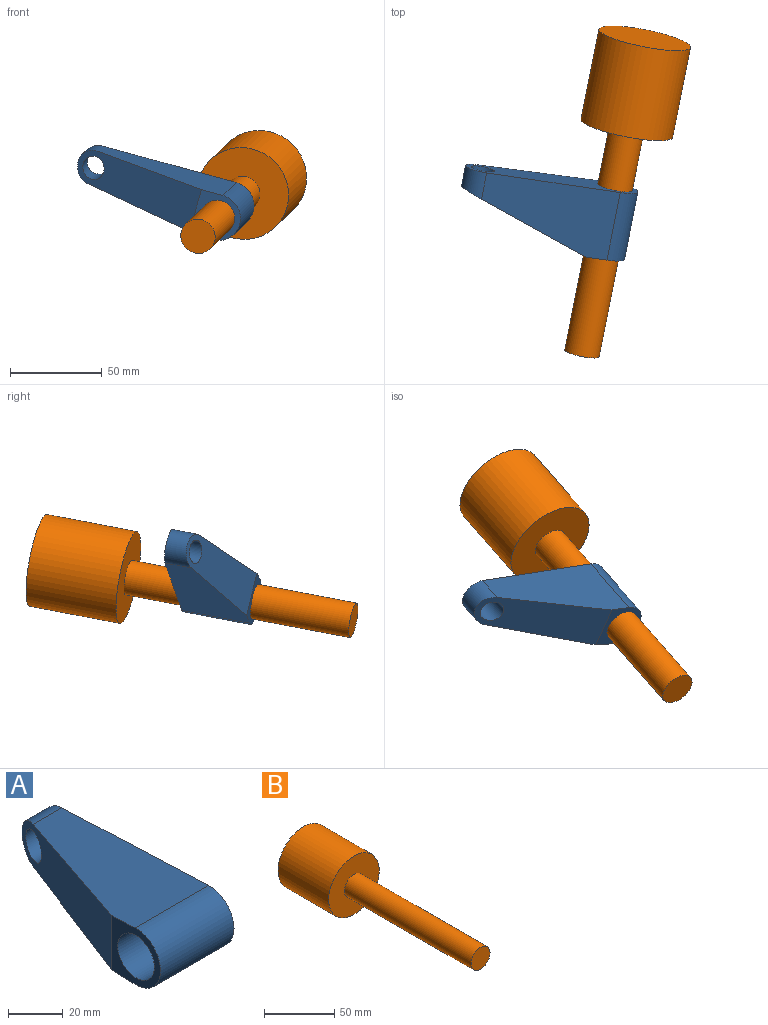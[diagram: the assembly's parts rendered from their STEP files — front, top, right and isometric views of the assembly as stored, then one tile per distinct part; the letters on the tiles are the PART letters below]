
ASSEMBLY  parts=2 mates=1
PART A: 9 faces, bbox 38.1x98.4x25.4 mm
  f0: plane 76.07x38.1mm, normal (0,0.04,1), area 2157mm2, adj f3,f4,f5,f7,f8
  f1: plane 76.07x38.1mm, normal (0,0.04,-1), area 2157mm2, adj f3,f4,f5,f7,f8
  f2: cylinder r=6.35mm len=17.3mm, axis (-1,0,0), area 598mm2, adj f7,f8
  f3: cylinder r=9.53mm len=19.03mm, axis (-1,0,0), area 370.6mm2, adj f0,f1,f7,f8
  f4: plane 25.4x25.4mm, normal (-1,0,0), area 284.5mm2, adj f0,f1,f5,f6,f8
  f5: cylinder r=12.7mm len=38.1mm, axis (-1,0,0), area 1560.5mm2, adj f0,f1,f4,f7
  f6: cylinder r=9.53mm len=38.1mm, axis (-1,0,0), area 2280.2mm2, adj f4,f7
  f7: plane 98.43x25.4mm, normal (1,0,0), area 1679.2mm2, adj f0,f1,f2,f3,f5,f6
  f8: plane 73.03x26.58mm, normal (-0.94,0.34,0), area 1484.2mm2, adj f0,f1,f2,f3,f4
PART B: 5 faces, bbox 50.8x177.8x50.8 mm
  f0: cylinder r=9.53mm len=127mm, axis (0,1,0), area 7600.6mm2, adj f1,f4
  f1: plane 19.05x19.05mm, normal (0,-1,0), area 285mm2, adj f0
  f2: cylinder r=25.4mm len=50.8mm, axis (0,-1,0), area 8107.3mm2, adj f3,f4
  f3: plane 50.8x50.8mm, normal (0,1,0), area 2026.8mm2, adj f2
  f4: plane 50.8x50.8mm, normal (0,-1,0), area 1741.8mm2, adj f0,f2
PLACE A rot(axis=(0.27,0.04,0.96),82.5deg) t=(-45.09,-324.45,-251.77)mm
PLACE B rot(axis=(0.54,0.73,-0.42),22.7deg) t=(-31.36,-255.6,-238.65)mm
MATE slider A.f6 <-> B.f0  axis (0.19,0.96,0.18) through (-37.76,-287.72,-244.77)mm
